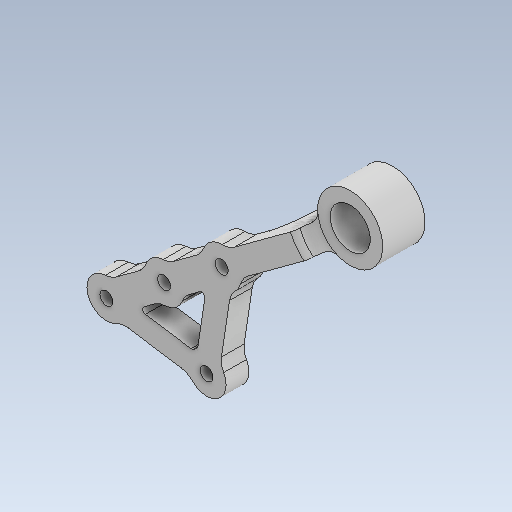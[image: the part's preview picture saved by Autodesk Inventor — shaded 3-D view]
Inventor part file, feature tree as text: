
AUTODESK INVENTOR PART (.ipt)
format: ipt  version: 2020 (Build 240168000, 168)  size: 355,840 bytes
history: native  units: mm
features: extrude x8, sketch x8, fillet x7, projected_geometry x7, other x4, reference x2, plane x1, thicken_offset x1
ambient origin geometry x8: Origin, YZ Plane, XZ Plane, XY Plane, X Axis, Y Axis, Z Axis, Center Point
bodies: Solid1 (feature_tree)
feature tree (38):
  extrude  "Extrusion1"  Depth=10.0mm
  sketch  "Sketch2"  dims[d2=2.0mm d3=11.0mm]
  plane  "Work Plane1"
  extrude  "Extrusion2"  Depth=2.0mm
  thicken_offset  "Thicken1"
  extrude  "Extrusion3"  Depth=4.0mm
  extrude  "Extrusion4"  Depth=3.5mm TaperAngle=0.0deg
  extrude  "Extrusion5"  Depth=10.0mm TaperAngle=0.0deg
  extrude  "Extrusion6"  Depth=1.5mm
  fillet  "Fillet1"  Radius=6.0mm
  fillet  "Fillet2"  Radius=6.0mm
  fillet  "Fillet3"  Radius=7.0mm
  fillet  "Fillet4"  Radius=6.15mm
  fillet  "Fillet5"  Radius=9.0mm
  extrude  "Extrusion7"  Depth=2.0mm TaperAngle=0.0deg
  extrude  "Extrusion8"  Depth=2.0mm TaperAngle=0.0deg
  fillet  "Fillet6"  Radius=4.0mm
  fillet  "Fillet7"  Radius=2.0mm
  sketch  "Sketch1"  dims[d0=10.0mm d1=11.0mm]
  reference  "Reference1"
  reference  "Reference2"
  projected_geometry  "Projected Loop1"
  sketch  "Sketch3"  dims[d4=2.0mm d5=4.0mm]
  projected_geometry  "Projected Loop2"
  sketch  "Sketch4"  dims[d6=3.5mm d7=7.0mm d8=0.0mm]
  projected_geometry  "Projected Loop3"
  sketch  "Sketch5"  dims[d9=10.0mm d10=7.0mm d11=0.0mm]
  projected_geometry  "Projected Loop4"
  sketch  "Sketch6"  dims[d12=1.5mm d13=1.5mm d14=6.0mm d15=6.0mm d16=7.0mm d17=0.0mm d18=6.15mm d19=9.0mm d20=0.0mm]
  projected_geometry  "Projected Loop5"
  sketch  "Sketch7"  dims[d21=2.0mm d22=9.0mm d23=0.0mm]
  projected_geometry  "Projected Loop6"
  sketch  "Sketch8"  dims[d24=14.0mm d25=2.0mm d26=0.0mm d30=4.0mm d31=2.0mm d32=2.0mm d33=2.0mm d34=1.0mm d35=6.0mm d36=3.5mm d37=0.0mm d38=11.0mm d39=2.0mm d40=3.5mm d42=6.0mm d43=3.5mm d44=6.0mm d45=3.5mm d46=0.0mm d47=3.0mm d48=0.5mm]
  projected_geometry  "Projected Loop7"
  parser-record x1  (decoder bookkeeping rows leaked as tree rows — omitted from the tree; the rows remain in map.json)
  other  "leg_1.iam"
  other  "leg_link_3:1"
  other  "reducer_1:1"
note: 1 file-system path scrubbed to <path> (originals preserved in map.json)
